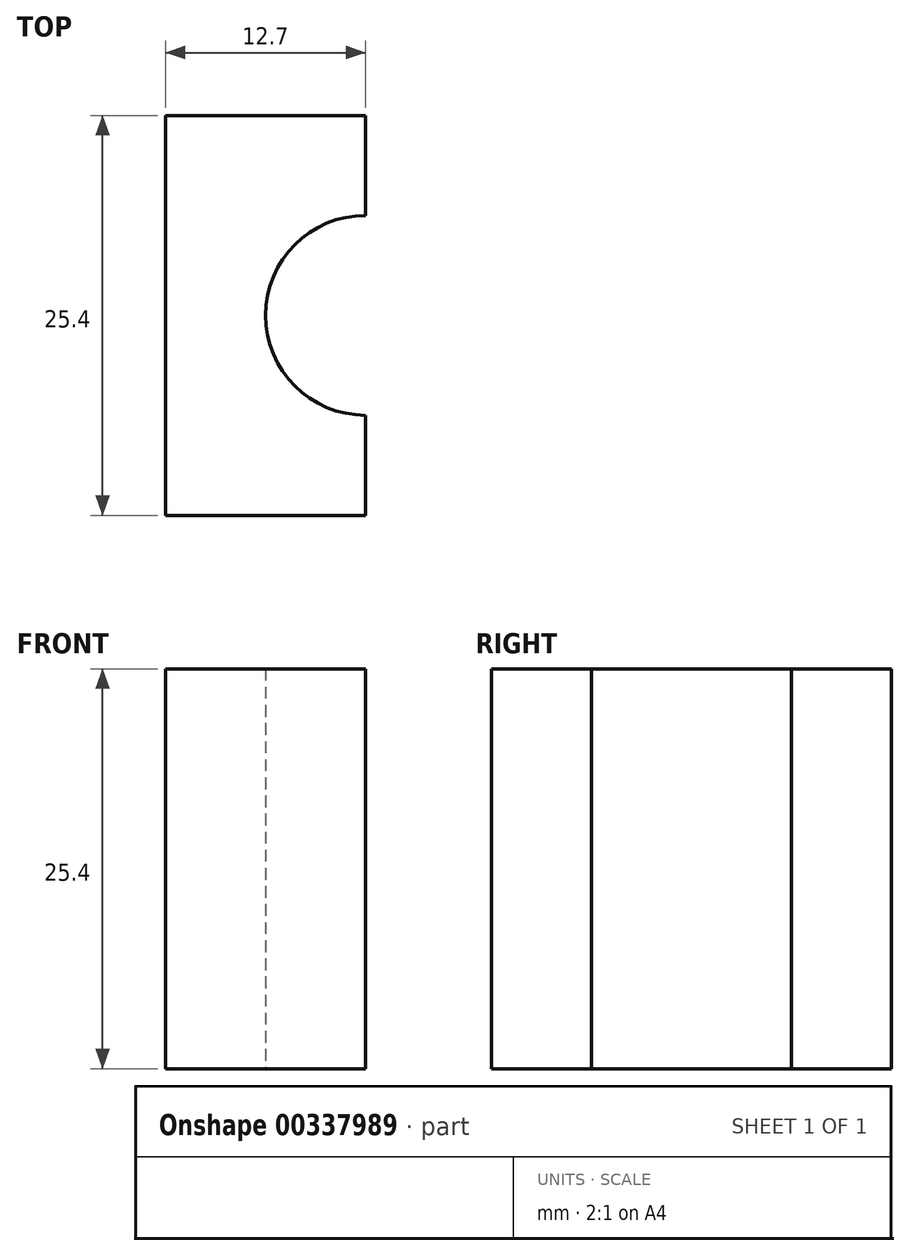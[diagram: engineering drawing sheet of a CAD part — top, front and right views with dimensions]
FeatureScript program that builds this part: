
annotation { "Feature Type Name" : "Feature", "Feature Type Description" : "" }
export const myFeature = defineFeature(function(context is Context, id is Id, definition is map)
    precondition{}
    {
        {
            var Q0;
            Q0=qCreatedBy(makeId("Top.planeOp"),FACE);
            var sketch = newSketch(context, id + "F0", { "sketchPlane" : qUnion([Q0])});
            skLineSegment(sketch, "E0.bottom", {"start": v(0, 0) * mm, "end": v(12.7, 0) * mm});
            skLineSegment(sketch, "E0.top", {"start": v(0, 25.4) * mm, "end": v(12.7, 25.4) * mm});
            skLineSegment(sketch, "E0.left", {"start": v(0, 0) * mm, "end": v(0, 25.4) * mm});
            skLineSegment(sketch, "E0.right", {"start": v(12.7, 0) * mm, "end": v(12.7, 6.35) * mm});
            skArc(sketch, "E1", {"start": v(12.7, 19.05) * mm, "mid": v(6.35, 12.7) * mm, "end": v(12.7, 6.35) * mm});
            skLineSegment(sketch, "E2.trimOffspring", {"start": v(12.7, 19.05) * mm, "end": v(12.7, 25.4) * mm});
            skSolve(sketch);
        }
        {
            var Q0;
            Q0=makeQuery(id+"F0.imprint","IMPRINT",FACE,{"disambiguationData":[TD([[makeQuery(id+"F0.imprint","IMPRINT",EDGE,{"derivedFrom":sQuery(id+"F0.wireOp",EDGE,"E0.bottom")}),1.0]])]});
            extrude(context, id + "F1", {"entities" : qUnion([Q0]), "depth" : 25.4 * mm, "offsetDistance" : 25.4 * mm});
        }
    });
